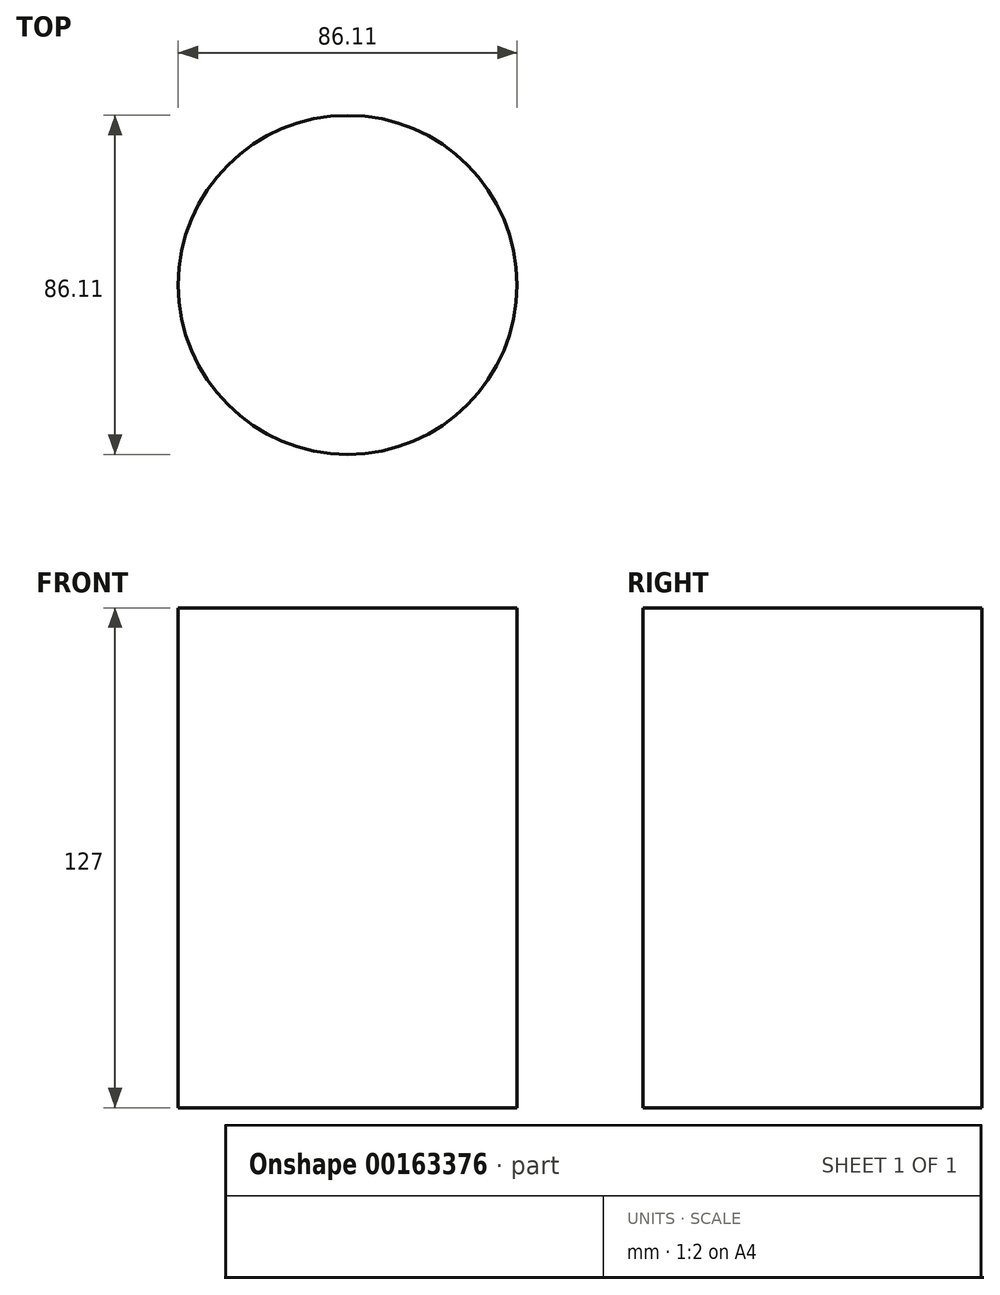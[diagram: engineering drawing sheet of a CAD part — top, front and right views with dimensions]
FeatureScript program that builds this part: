
annotation { "Feature Type Name" : "Feature", "Feature Type Description" : "" }
export const myFeature = defineFeature(function(context is Context, id is Id, definition is map)
    precondition{}
    {
        {
            var Q0;
            Q0=qCreatedBy(makeId("Top.planeOp"),FACE);
            var sketch = newSketch(context, id + "F0", { "sketchPlane" : qUnion([Q0])});
            skCircle(sketch, "E0", {"center": v(40.28, -40.1) * mm, "radius": 43.05 * mm});
            skSolve(sketch);
        }
        {
            var Q0;
            Q0=makeQuery(id+"F0.imprint","IMPRINT",FACE,{"disambiguationData":[TD([[makeQuery(id+"F0.imprint","IMPRINT",EDGE,{"derivedFrom":sQuery(id+"F0.wireOp",EDGE,"E0")}),1.0]])]});
            extrude(context, id + "F1", {"entities" : qUnion([Q0]), "depth" : 127 * mm});
        }
    });
